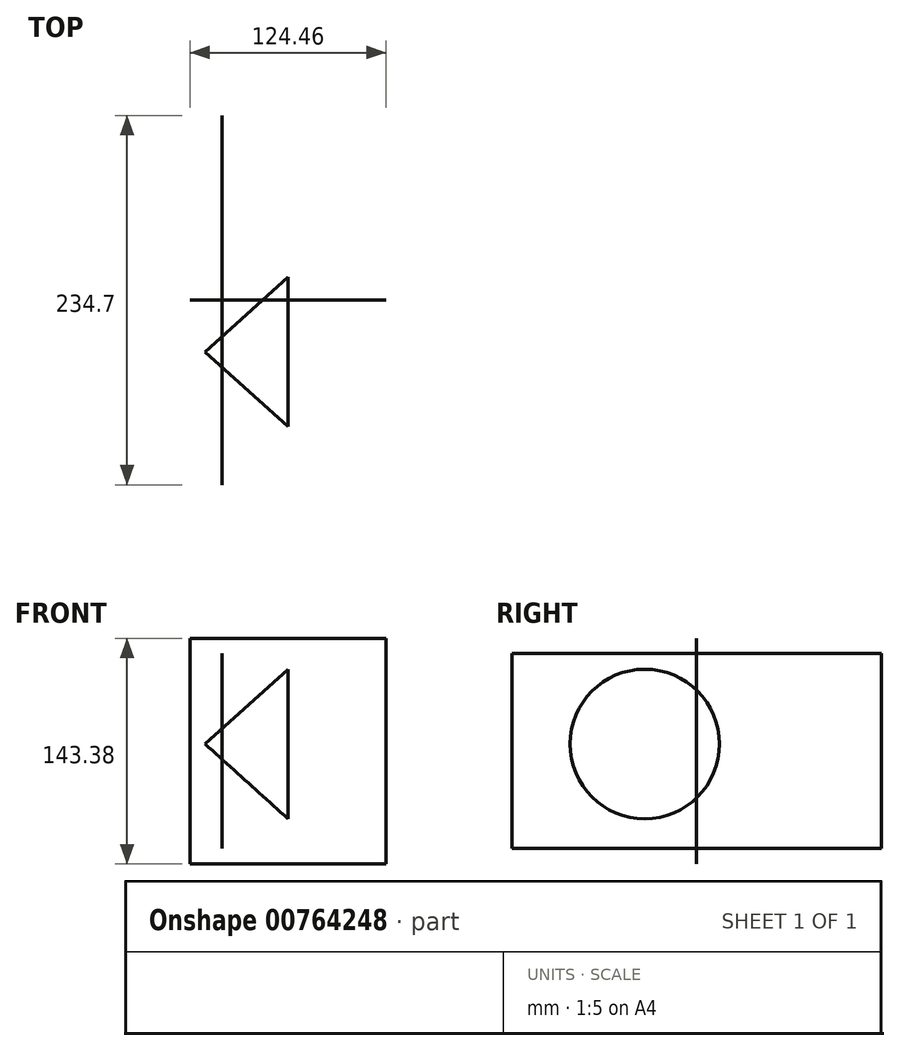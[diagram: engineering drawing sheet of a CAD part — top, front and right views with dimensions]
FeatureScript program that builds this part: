
annotation { "Feature Type Name" : "Feature", "Feature Type Description" : "" }
export const myFeature = defineFeature(function(context is Context, id is Id, definition is map)
    precondition{}
    {
        {
            var Q0;
            Q0=qCreatedBy(makeId("Front.planeOp"),FACE);
            var sketch = newSketch(context, id + "F0", { "sketchPlane" : qUnion([Q0])});
            skLineSegment(sketch, "E0", {"start": v(-52.63, 0) * mm, "end": v(0, 0) * mm});
            skLineSegment(sketch, "E1", {"start": v(0, 0) * mm, "end": v(0, 47.47) * mm});
            skLineSegment(sketch, "E2", {"start": v(0, 47.47) * mm, "end": v(-52.63, 0) * mm});
            skSolve(sketch);
        }
        {
            var Q0;
            Q0=sQuery(id+"F0.wireOp",EDGE,"E2");
            var Q1;
            Q1=sQuery(id+"F0.wireOp",EDGE,"E0");
            revolve(context, id + "F1", {"bodyType" : ToolBodyType.SURFACE, "surfaceOperationType" : NewSurfaceOperationType.NEW, "surfaceEntities" : qUnion([Q0]), "axis" : qUnion([Q1]), "revolveType" : RevolveType.FULL});
        }
        {
            var Q0;
            Q0=qCreatedBy(makeId("Right.planeOp"),FACE);
            var sketch = newSketch(context, id + "F2", { "sketchPlane" : qUnion([Q0])});
            skLineSegment(sketch, "E3", {"start": v(32.95, -76.3) * mm, "end": v(32.95, 67.08) * mm});
            skSolve(sketch);
        }
        {
            var Q0;
            Q0=sQuery(id+"F2.wireOp",EDGE,"E3");
            extrude(context, id + "F3", {"bodyType" : ToolBodyType.SURFACE, "surfaceEntities" : qUnion([Q0]), "endBound" : BoundingType.SYMMETRIC, "depth" : 124.46 * mm, "offsetDistance" : 25.4 * mm});
        }
        {
            var Q0;
            Q0=makeQuery(id+"F3.opExtrude","SWEPT_FACE",FACE,{"disambiguationData":[OSD([sQuery(id+"F2.wireOp",EDGE,"E3")])]});
            var sketch = newSketch(context, id + "F4", { "sketchPlane" : qUnion([Q0])});
            skLineSegment(sketch, "E4", {"start": v(41.78, -66.18) * mm, "end": v(41.78, 57.41) * mm});
            skSolve(sketch);
        }
        {
            var Q0;
            Q0=sQuery(id+"F4.wireOp",EDGE,"E4");
            extrude(context, id + "F5", {"bodyType" : ToolBodyType.SURFACE, "surfaceEntities" : qUnion([Q0]), "endBound" : BoundingType.SYMMETRIC, "depth" : 234.7 * mm, "offsetDistance" : 25.4 * mm});
        }
    });
